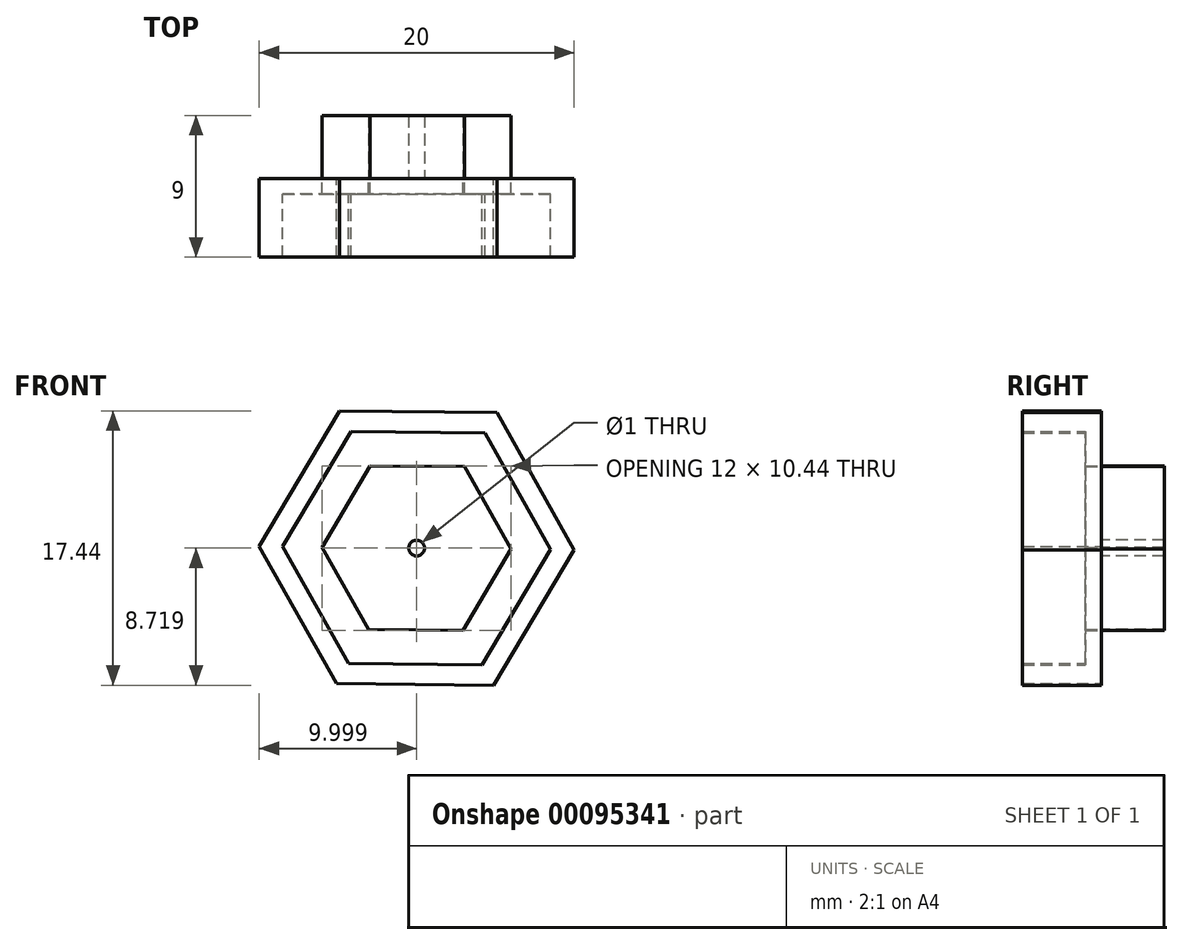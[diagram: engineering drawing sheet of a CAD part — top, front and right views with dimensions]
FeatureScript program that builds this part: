
annotation { "Feature Type Name" : "Feature", "Feature Type Description" : "" }
export const myFeature = defineFeature(function(context is Context, id is Id, definition is map)
    precondition{}
    {
        {
            var Q0;
            Q0=qCreatedBy(makeId("Front.planeOp"),FACE);
            var sketch = newSketch(context, id + "F0", { "sketchPlane" : qUnion([Q0])});
            skCircle(sketch, "E0.cCircle", {"center": v(-47.72, 29.72) * mm, "radius": 7.36 * mm, "construction": true});
            skLineSegment(sketch, "E0.0", {"start": v(-39.22, 29.62) * mm, "end": v(-43.56, 22.3) * mm});
            skLineSegment(sketch, "E0.1", {"start": v(-43.56, 22.3) * mm, "end": v(-52.06, 22.4) * mm});
            skLineSegment(sketch, "E0.2", {"start": v(-52.06, 22.4) * mm, "end": v(-56.22, 29.82) * mm});
            skLineSegment(sketch, "E0.3", {"start": v(-56.22, 29.82) * mm, "end": v(-51.89, 37.13) * mm});
            skLineSegment(sketch, "E0.4", {"start": v(-51.89, 37.13) * mm, "end": v(-43.39, 37.03) * mm});
            skLineSegment(sketch, "E0.5", {"start": v(-43.39, 37.03) * mm, "end": v(-39.22, 29.62) * mm});
            skPoint(sketch, "E0.0.midPoint", {"position": v(-41.39, 25.96) * mm});
            skCircle(sketch, "E1.cCircle", {"center": v(-47.72, 29.72) * mm, "radius": 5.2 * mm, "construction": true});
            skLineSegment(sketch, "E1.0", {"start": v(-41.72, 29.67) * mm, "end": v(-44.77, 24.5) * mm});
            skLineSegment(sketch, "E1.1", {"start": v(-44.77, 24.5) * mm, "end": v(-50.77, 24.55) * mm});
            skLineSegment(sketch, "E1.2", {"start": v(-50.77, 24.55) * mm, "end": v(-53.72, 29.77) * mm});
            skLineSegment(sketch, "E1.3", {"start": v(-53.72, 29.77) * mm, "end": v(-50.68, 34.94) * mm});
            skLineSegment(sketch, "E1.4", {"start": v(-50.68, 34.94) * mm, "end": v(-44.68, 34.89) * mm});
            skLineSegment(sketch, "E1.5", {"start": v(-44.68, 34.89) * mm, "end": v(-41.72, 29.67) * mm});
            skPoint(sketch, "E1.0.midPoint", {"position": v(-43.24, 27.08) * mm});
            skCircle(sketch, "E2.cCircle", {"center": v(-47.72, 29.72) * mm, "radius": 8.66 * mm, "construction": true});
            skLineSegment(sketch, "E2.0", {"start": v(-37.72, 29.6) * mm, "end": v(-42.82, 21) * mm});
            skLineSegment(sketch, "E2.1", {"start": v(-42.82, 21) * mm, "end": v(-52.82, 21.12) * mm});
            skLineSegment(sketch, "E2.2", {"start": v(-52.82, 21.12) * mm, "end": v(-57.72, 29.83) * mm});
            skLineSegment(sketch, "E2.3", {"start": v(-57.72, 29.83) * mm, "end": v(-52.62, 38.44) * mm});
            skLineSegment(sketch, "E2.4", {"start": v(-52.62, 38.44) * mm, "end": v(-42.62, 38.32) * mm});
            skLineSegment(sketch, "E2.5", {"start": v(-42.62, 38.32) * mm, "end": v(-37.72, 29.6) * mm});
            skPoint(sketch, "E2.0.midPoint", {"position": v(-40.27, 25.3) * mm});
            skCircle(sketch, "E3", {"center": v(-47.72, 29.72) * mm, "radius": 0.5 * mm});
            skSolve(sketch);
        }
        {
            var Q0;
            Q0 = qSketchRegion(id + "F0", true);
            extrude(context, id + "F1", {"entities" : qUnion([Q0]), "depth" : 5 * mm});
        }
        {
            var Q0;
            Q0=makeQuery(id+"F0.imprint","IMPRINT",FACE,{"disambiguationData":[TD([[makeQuery(id+"F0.imprint","IMPRINT",EDGE,{"derivedFrom":sQuery(id+"F0.wireOp",EDGE,"E0.0")}),-1.0]])]});
            extrude(context, id + "F2", {"entities" : qUnion([Q0]), "operationType" : NewBodyOperationType.ADD, "depth" : 1 * mm});
        }
        {
            var Q0;
            Q0=makeQuery(id+"F0.imprint","IMPRINT",FACE,{"disambiguationData":[TD([[makeQuery(id+"F0.imprint","IMPRINT",EDGE,{"derivedFrom":sQuery(id+"F0.wireOp",EDGE,"E1.0")}),-1.0]])]});
            extrude(context, id + "F3", {"entities" : qUnion([Q0]), "oppositeDirection" : true, "depth" : 4 * mm});
        }
    });
